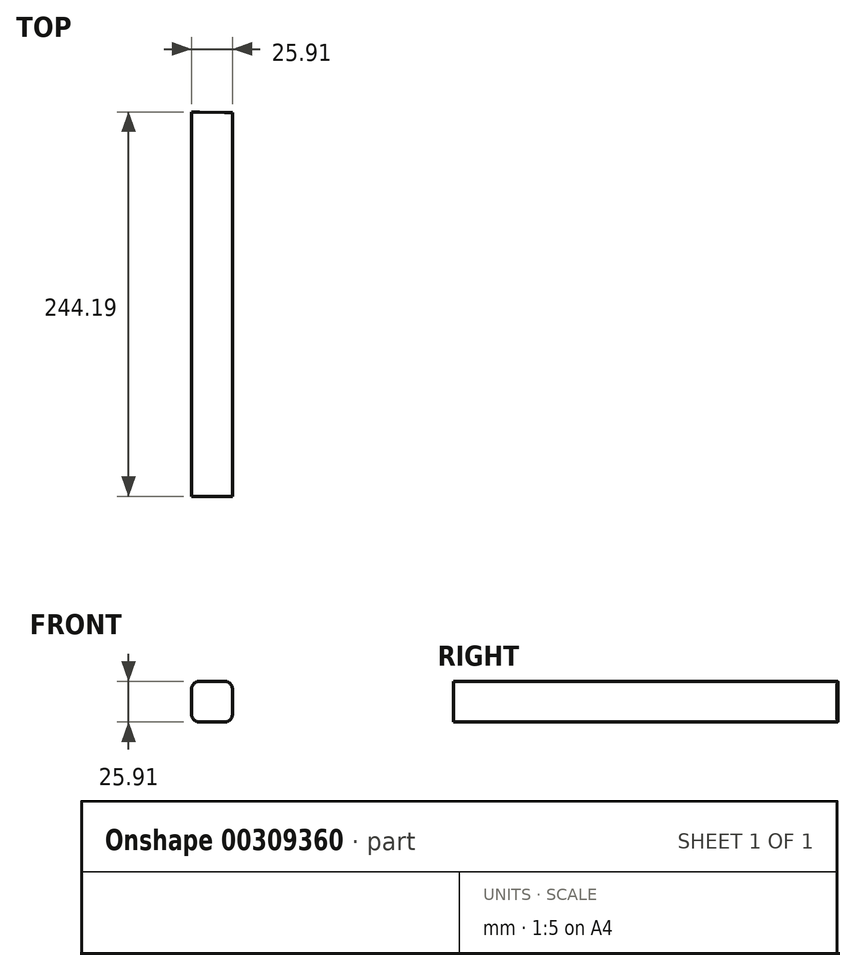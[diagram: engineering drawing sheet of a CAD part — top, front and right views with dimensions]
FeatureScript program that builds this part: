
annotation { "Feature Type Name" : "Feature", "Feature Type Description" : "" }
export const myFeature = defineFeature(function(context is Context, id is Id, definition is map)
    precondition{}
    {
        {
            var Q0;
            Q0=qCreatedBy(makeId("Top.planeOp"),FACE);
            var sketch = newSketch(context, id + "F0", { "sketchPlane" : qUnion([Q0])});
            skLineSegment(sketch, "E0", {"start": v(26.44, 125.05) * mm, "end": v(26.44, -118.7) * mm});
            skLineSegment(sketch, "E1", {"start": v(26.44, -118.7) * mm, "end": v(0.53, -118.7) * mm});
            skLineSegment(sketch, "E2", {"start": v(0.53, -118.7) * mm, "end": v(0.53, 125.48) * mm});
            skLineSegment(sketch, "E3", {"start": v(26.44, 125.05) * mm, "end": v(0.53, 125.48) * mm});
            skSolve(sketch);
        }
        {
            var Q0;
            Q0=makeQuery(id+"F0.imprint","IMPRINT",FACE,{"disambiguationData":[TD([[makeQuery(id+"F0.imprint","IMPRINT",EDGE,{"derivedFrom":sQuery(id+"F0.wireOp",EDGE,"E0")}),-1.0]])]});
            var Q1;
            Q1=sQuery(id+"F0.wireOp",EDGE,"E3");
            var Q2;
            Q2=sQuery(id+"F0.wireOp",EDGE,"E0");
            var Q3;
            Q3=sQuery(id+"F0.wireOp",EDGE,"E2");
            var Q4;
            Q4=sQuery(id+"F0.wireOp",EDGE,"E1");
            extrude(context, id + "F1", {"entities" : qUnion([Q0]), "surfaceEntities" : qUnion([Q1, Q2, Q3, Q4]), "depth" : 25.9 * mm});
        }
        {
            var Q0;
            Q0=makeQuery(id+"F1.opExtrude","CAP_EDGE",EDGE,{"disambiguationData":[OSD([sQuery(id+"F0.wireOp",EDGE,"E2")])],"isStart":false});
            var Q1;
            Q1=makeQuery(id+"F1.opExtrude","CAP_EDGE",EDGE,{"disambiguationData":[OSD([sQuery(id+"F0.wireOp",EDGE,"E0")])],"isStart":false});
            var Q2;
            Q2=makeQuery(id+"F1.opExtrude","CAP_EDGE",EDGE,{"disambiguationData":[OSD([sQuery(id+"F0.wireOp",EDGE,"E2")])],"isStart":true});
            var Q3;
            Q3=makeQuery(id+"F1.opExtrude","CAP_EDGE",EDGE,{"disambiguationData":[OSD([sQuery(id+"F0.wireOp",EDGE,"E0")])],"isStart":true});
            fillet(context, id + "F2", {"entities" : qUnion([Q0, Q1, Q2, Q3]), "radius" : 5.08 * mm, "tangentPropagation" : true, "allowEdgeOverflow" : false});
        }
    });
